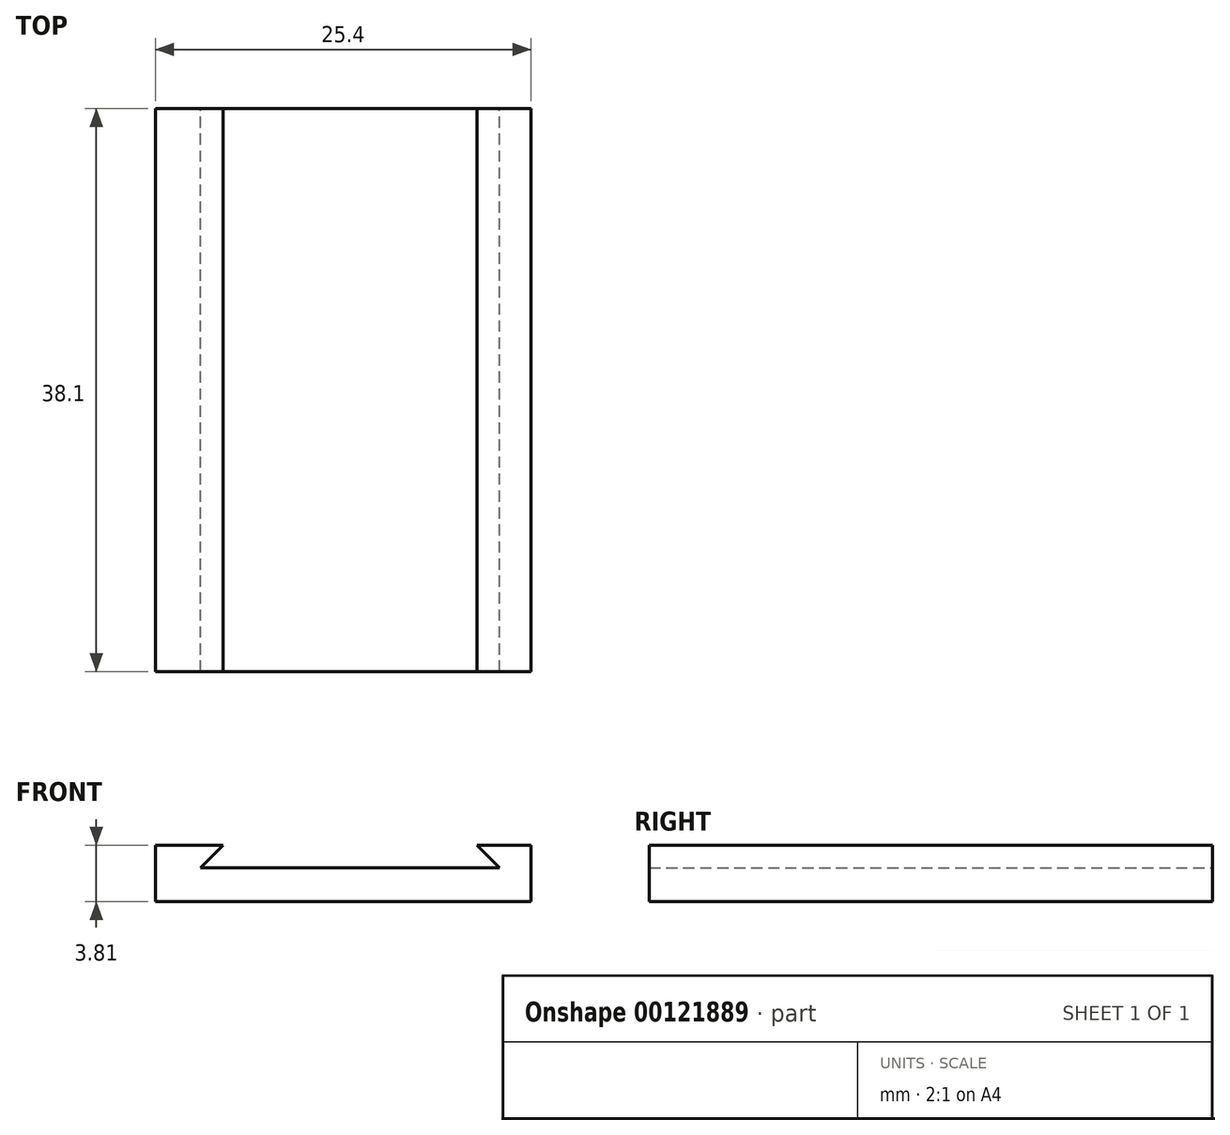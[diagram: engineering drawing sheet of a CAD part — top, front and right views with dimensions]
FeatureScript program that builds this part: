
annotation { "Feature Type Name" : "Feature", "Feature Type Description" : "" }
export const myFeature = defineFeature(function(context is Context, id is Id, definition is map)
    precondition{}
    {
        {
            var Q0;
            Q0=qCreatedBy(makeId("Front.planeOp"),FACE);
            var sketch = newSketch(context, id + "F0", { "sketchPlane" : qUnion([Q0])});
            skLineSegment(sketch, "E0", {"start": v(-19.13, -0.52) * mm, "end": v(-19.13, 3.29) * mm});
            skLineSegment(sketch, "E1", {"start": v(-19.13, 3.29) * mm, "end": v(-14.56, 3.29) * mm});
            skLineSegment(sketch, "E2", {"start": v(-14.56, 3.29) * mm, "end": v(-16.07, 1.78) * mm});
            skLineSegment(sketch, "E3", {"start": v(-16.07, 1.78) * mm, "end": v(4.14, 1.78) * mm});
            skLineSegment(sketch, "E4", {"start": v(4.14, 1.78) * mm, "end": v(2.63, 3.29) * mm});
            skLineSegment(sketch, "E5", {"start": v(2.63, 3.29) * mm, "end": v(6.27, 3.29) * mm});
            skLineSegment(sketch, "E6", {"start": v(6.27, 3.29) * mm, "end": v(6.27, -0.52) * mm});
            skLineSegment(sketch, "E7", {"start": v(6.27, -0.52) * mm, "end": v(-19.13, -0.52) * mm});
            skSolve(sketch);
        }
        {
            var Q0;
            Q0 = qSketchRegion(id + "F0", true);
            extrude(context, id + "F1", {"entities" : qUnion([Q0]), "depth" : 38.1 * mm});
        }
    });
